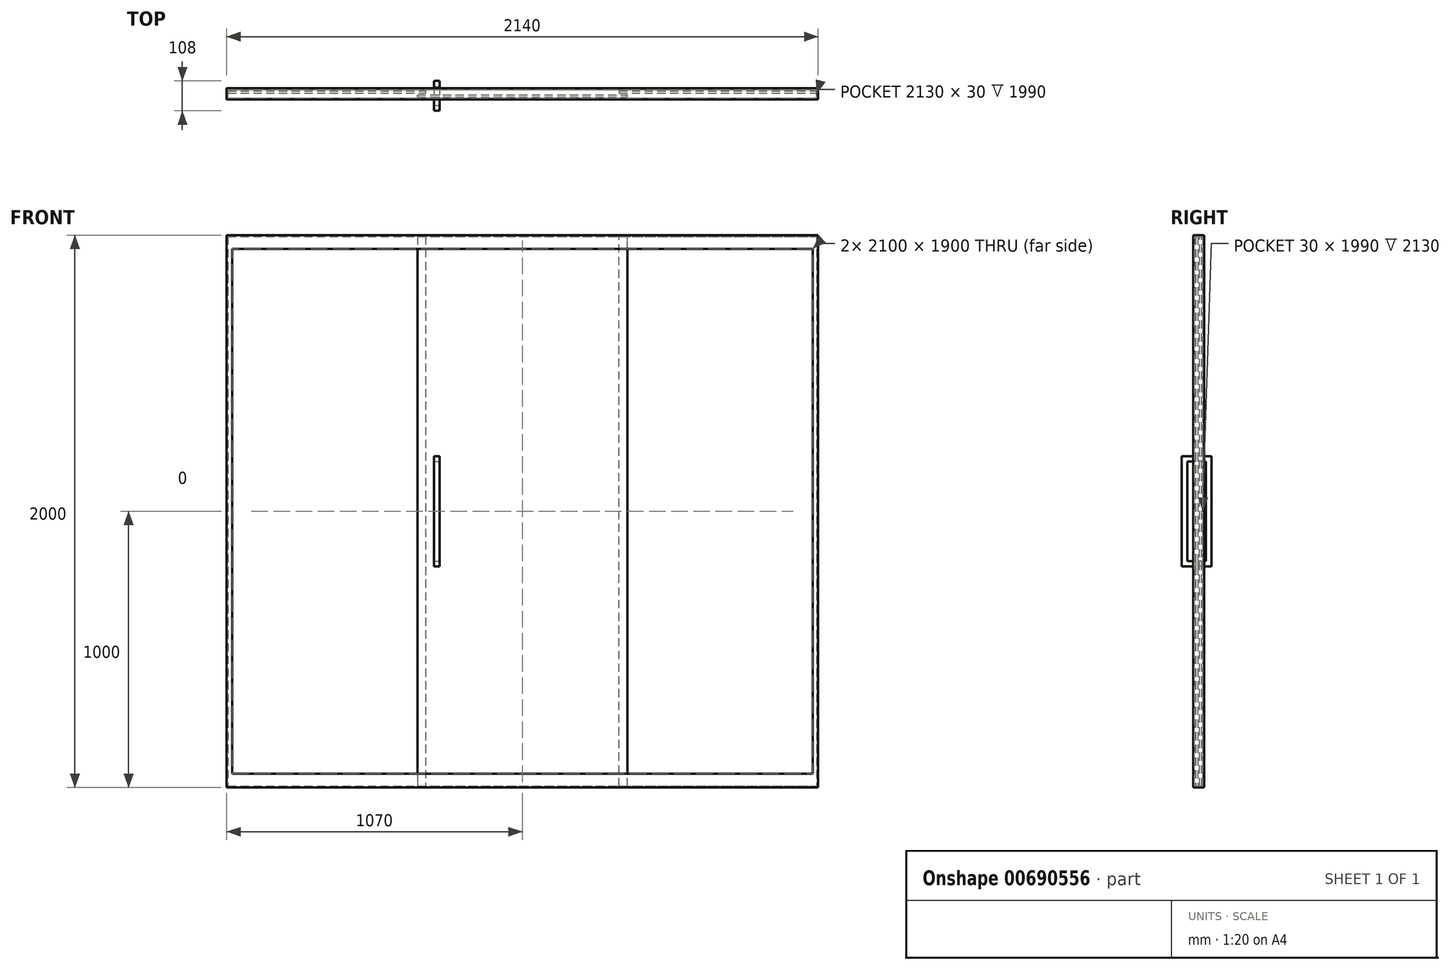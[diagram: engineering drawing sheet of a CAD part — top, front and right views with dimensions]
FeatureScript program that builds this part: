
annotation { "Feature Type Name" : "Feature", "Feature Type Description" : "" }
export const myFeature = defineFeature(function(context is Context, id is Id, definition is map)
    precondition{}
    {
        {
            var Q0;
            Q0=qCreatedBy(makeId("Front.planeOp"),FACE);
            var sketch = newSketch(context, id + "F0", { "sketchPlane" : qUnion([Q0])});
            skLineSegment(sketch, "E0.bottom", {"start": v(0, 0) * mm, "end": v(2140, 0) * mm});
            skLineSegment(sketch, "E0.top", {"start": v(0, 2000) * mm, "end": v(2140, 2000) * mm});
            skLineSegment(sketch, "E0.left", {"start": v(0, 0) * mm, "end": v(0, 2000) * mm});
            skLineSegment(sketch, "E0.right", {"start": v(2140, 0) * mm, "end": v(2140, 2000) * mm});
            skLineSegment(sketch, "E1.bottom", {"start": v(5, 1995) * mm, "end": v(2135, 1995) * mm});
            skLineSegment(sketch, "E1.top", {"start": v(5, 5) * mm, "end": v(2135, 5) * mm});
            skLineSegment(sketch, "E1.left", {"start": v(5, 1995) * mm, "end": v(5, 5) * mm});
            skLineSegment(sketch, "E1.right", {"start": v(2135, 1995) * mm, "end": v(2135, 5) * mm});
            skLineSegment(sketch, "E2.bottom", {"start": v(20, 1950) * mm, "end": v(2120, 1950) * mm});
            skLineSegment(sketch, "E2.top", {"start": v(20, 50) * mm, "end": v(2120, 50) * mm});
            skLineSegment(sketch, "E2.left", {"start": v(20, 1950) * mm, "end": v(20, 50) * mm});
            skLineSegment(sketch, "E2.right", {"start": v(2120, 1950) * mm, "end": v(2120, 50) * mm});
            skLineSegment(sketch, "E3", {"start": v(720, 1995) * mm, "end": v(720, 5) * mm});
            skLineSegment(sketch, "E4", {"start": v(1420, 5) * mm, "end": v(1420, 1995) * mm});
            skLineSegment(sketch, "E5", {"start": v(720, 1000) * mm, "end": v(5, 1000) * mm, "construction": true});
            skLineSegment(sketch, "E6", {"start": v(1420, 1000) * mm, "end": v(2135, 1000) * mm, "construction": true});
            skLineSegment(sketch, "E7", {"start": v(690, 1995) * mm, "end": v(690, 5) * mm});
            skLineSegment(sketch, "E8", {"start": v(1450, 5) * mm, "end": v(1450, 1995) * mm});
            skSolve(sketch);
        }
        {
            var Q0;
            {var subQ4=sQuery(id+"F0.wireOp",EDGE,"E1.left");Q0=makeQuery(id+"F0.imprint","IMPRINT",FACE,{"disambiguationData":[TD([[makeQuery(id+"F0.imprint","IMPRINT",EDGE,{"derivedFrom":subQ4}),1.0]])]});}
            var Q1;
            Q1=makeQuery(id+"F0.imprint","IMPRINT",FACE,{"disambiguationData":[TD([[makeQuery(id+"F0.imprint","IMPRINT",EDGE,{"derivedFrom":sQuery(id+"F0.wireOp",EDGE,"E0.bottom")}),1.0]])]});
            var Q2;
            {var subQ0=sQuery(id+"F0.wireOp",EDGE,"E3");var subQ1=sQuery(id+"F0.wireOp",EDGE,"E1.bottom");var subQ2=makeQuery(id+"F0.imprint","INTERSECT",VERTEX,{"derivedFrom":[subQ1,subQ0]});Q2=makeQuery(id+"F0.imprint","IMPRINT",FACE,{"disambiguationData":[TD([[makeQuery(id+"F0.imprint","IMPRINT",EDGE,{"disambiguationData":[TD([[subQ2,1.0]])],"derivedFrom":subQ1}),-1.0]])]});}
            var Q3;
            {var subQ0=sQuery(id+"F0.wireOp",EDGE,"E3");var subQ1=sQuery(id+"F0.wireOp",EDGE,"E1.bottom");var subQ2=makeQuery(id+"F0.imprint","INTERSECT",VERTEX,{"derivedFrom":[subQ1,subQ0]});Q3=makeQuery(id+"F0.imprint","IMPRINT",FACE,{"disambiguationData":[TD([[makeQuery(id+"F0.imprint","IMPRINT",EDGE,{"disambiguationData":[TD([[subQ2,-1.0]])],"derivedFrom":subQ1}),-1.0]])]});}
            var Q4;
            {var subQ4=sQuery(id+"F0.wireOp",EDGE,"E1.right");Q4=makeQuery(id+"F0.imprint","IMPRINT",FACE,{"disambiguationData":[TD([[makeQuery(id+"F0.imprint","IMPRINT",EDGE,{"derivedFrom":subQ4}),-1.0]])]});}
            var Q5;
            {var subQ0=sQuery(id+"F0.wireOp",EDGE,"E4");var subQ1=sQuery(id+"F0.wireOp",EDGE,"E1.bottom");var subQ2=makeQuery(id+"F0.imprint","INTERSECT",VERTEX,{"derivedFrom":[subQ1,subQ0]});Q5=makeQuery(id+"F0.imprint","IMPRINT",FACE,{"disambiguationData":[TD([[makeQuery(id+"F0.imprint","IMPRINT",EDGE,{"disambiguationData":[TD([[subQ2,-1.0]])],"derivedFrom":subQ1}),-1.0]])]});}
            var Q6;
            {var subQ0=sQuery(id+"F0.wireOp",EDGE,"E3");var subQ1=sQuery(id+"F0.wireOp",EDGE,"E1.top");var subQ2=makeQuery(id+"F0.imprint","INTERSECT",VERTEX,{"derivedFrom":[subQ1,subQ0]});Q6=makeQuery(id+"F0.imprint","IMPRINT",FACE,{"disambiguationData":[TD([[makeQuery(id+"F0.imprint","IMPRINT",EDGE,{"disambiguationData":[TD([[subQ2,1.0]])],"derivedFrom":subQ1}),1.0]])]});}
            var Q7;
            {var subQ0=sQuery(id+"F0.wireOp",EDGE,"E3");var subQ1=sQuery(id+"F0.wireOp",EDGE,"E1.top");var subQ2=makeQuery(id+"F0.imprint","INTERSECT",VERTEX,{"derivedFrom":[subQ1,subQ0]});Q7=makeQuery(id+"F0.imprint","IMPRINT",FACE,{"disambiguationData":[TD([[makeQuery(id+"F0.imprint","IMPRINT",EDGE,{"disambiguationData":[TD([[subQ2,-1.0]])],"derivedFrom":subQ1}),1.0]])]});}
            var Q8;
            {var subQ0=sQuery(id+"F0.wireOp",EDGE,"E4");var subQ1=sQuery(id+"F0.wireOp",EDGE,"E1.top");var subQ2=makeQuery(id+"F0.imprint","INTERSECT",VERTEX,{"derivedFrom":[subQ1,subQ0]});Q8=makeQuery(id+"F0.imprint","IMPRINT",FACE,{"disambiguationData":[TD([[makeQuery(id+"F0.imprint","IMPRINT",EDGE,{"disambiguationData":[TD([[subQ2,-1.0]])],"derivedFrom":subQ1}),1.0]])]});}
            extrude(context, id + "F1", {"entities" : qUnion([Q0, Q1, Q2, Q3, Q4, Q5, Q6, Q7, Q8]), "depth" : 20 * mm, "offsetDistance" : 25 * mm, "hasSecondDirection" : true, "secondDirectionOppositeDirection" : true, "secondDirectionDepth" : 20 * mm});
        }
        {
            var Q0;
            {var subQ4=sQuery(id+"F0.wireOp",EDGE,"E1.left");Q0=makeQuery(id+"F0.imprint","IMPRINT",FACE,{"disambiguationData":[TD([[makeQuery(id+"F0.imprint","IMPRINT",EDGE,{"derivedFrom":subQ4}),1.0]])]});}
            var Q1;
            {var subQ0=sQuery(id+"F0.wireOp",EDGE,"E3");var subQ1=sQuery(id+"F0.wireOp",EDGE,"E1.bottom");var subQ2=makeQuery(id+"F0.imprint","INTERSECT",VERTEX,{"derivedFrom":[subQ1,subQ0]});Q1=makeQuery(id+"F0.imprint","IMPRINT",FACE,{"disambiguationData":[TD([[makeQuery(id+"F0.imprint","IMPRINT",EDGE,{"disambiguationData":[TD([[subQ2,1.0]])],"derivedFrom":subQ1}),-1.0]])]});}
            var Q2;
            {var subQ0=sQuery(id+"F0.wireOp",EDGE,"E3");var subQ1=sQuery(id+"F0.wireOp",EDGE,"E1.bottom");var subQ2=makeQuery(id+"F0.imprint","INTERSECT",VERTEX,{"derivedFrom":[subQ1,subQ0]});Q2=makeQuery(id+"F0.imprint","IMPRINT",FACE,{"disambiguationData":[TD([[makeQuery(id+"F0.imprint","IMPRINT",EDGE,{"disambiguationData":[TD([[subQ2,-1.0]])],"derivedFrom":subQ1}),-1.0]])]});}
            var Q3;
            {var subQ0=sQuery(id+"F0.wireOp",EDGE,"E4");var subQ1=sQuery(id+"F0.wireOp",EDGE,"E1.bottom");var subQ2=makeQuery(id+"F0.imprint","INTERSECT",VERTEX,{"derivedFrom":[subQ1,subQ0]});Q3=makeQuery(id+"F0.imprint","IMPRINT",FACE,{"disambiguationData":[TD([[makeQuery(id+"F0.imprint","IMPRINT",EDGE,{"disambiguationData":[TD([[subQ2,-1.0]])],"derivedFrom":subQ1}),-1.0]])]});}
            var Q4;
            {var subQ4=sQuery(id+"F0.wireOp",EDGE,"E1.right");Q4=makeQuery(id+"F0.imprint","IMPRINT",FACE,{"disambiguationData":[TD([[makeQuery(id+"F0.imprint","IMPRINT",EDGE,{"derivedFrom":subQ4}),-1.0]])]});}
            var Q5;
            {var subQ0=sQuery(id+"F0.wireOp",EDGE,"E3");var subQ1=sQuery(id+"F0.wireOp",EDGE,"E1.top");var subQ2=makeQuery(id+"F0.imprint","INTERSECT",VERTEX,{"derivedFrom":[subQ1,subQ0]});Q5=makeQuery(id+"F0.imprint","IMPRINT",FACE,{"disambiguationData":[TD([[makeQuery(id+"F0.imprint","IMPRINT",EDGE,{"disambiguationData":[TD([[subQ2,1.0]])],"derivedFrom":subQ1}),1.0]])]});}
            var Q6;
            {var subQ0=sQuery(id+"F0.wireOp",EDGE,"E3");var subQ1=sQuery(id+"F0.wireOp",EDGE,"E1.top");var subQ2=makeQuery(id+"F0.imprint","INTERSECT",VERTEX,{"derivedFrom":[subQ1,subQ0]});Q6=makeQuery(id+"F0.imprint","IMPRINT",FACE,{"disambiguationData":[TD([[makeQuery(id+"F0.imprint","IMPRINT",EDGE,{"disambiguationData":[TD([[subQ2,-1.0]])],"derivedFrom":subQ1}),1.0]])]});}
            var Q7;
            {var subQ0=sQuery(id+"F0.wireOp",EDGE,"E4");var subQ1=sQuery(id+"F0.wireOp",EDGE,"E1.top");var subQ2=makeQuery(id+"F0.imprint","INTERSECT",VERTEX,{"derivedFrom":[subQ1,subQ0]});Q7=makeQuery(id+"F0.imprint","IMPRINT",FACE,{"disambiguationData":[TD([[makeQuery(id+"F0.imprint","IMPRINT",EDGE,{"disambiguationData":[TD([[subQ2,-1.0]])],"derivedFrom":subQ1}),1.0]])]});}
            extrude(context, id + "F2", {"entities" : qUnion([Q0, Q1, Q2, Q3, Q4, Q5, Q6, Q7]), "operationType" : NewBodyOperationType.REMOVE, "depth" : 15 * mm, "offsetDistance" : 25 * mm, "hasSecondDirection" : true, "secondDirectionOppositeDirection" : true, "secondDirectionDepth" : 15 * mm});
        }
        {
            var Q0;
            {var subQ0=sQuery(id+"F0.wireOp",EDGE,"E2.left");Q0=makeQuery(id+"F0.imprint","IMPRINT",FACE,{"disambiguationData":[TD([[makeQuery(id+"F0.imprint","IMPRINT",EDGE,{"derivedFrom":subQ0}),1.0]])]});}
            var Q1;
            {var subQ0=sQuery(id+"F0.wireOp",EDGE,"E2.right");Q1=makeQuery(id+"F0.imprint","IMPRINT",FACE,{"disambiguationData":[TD([[makeQuery(id+"F0.imprint","IMPRINT",EDGE,{"derivedFrom":subQ0}),-1.0]])]});}
            var Q2;
            {var subQ4=sQuery(id+"F0.wireOp",EDGE,"E1.right");Q2=makeQuery(id+"F0.imprint","IMPRINT",FACE,{"disambiguationData":[TD([[makeQuery(id+"F0.imprint","IMPRINT",EDGE,{"derivedFrom":subQ4}),-1.0]])]});}
            var Q3;
            {var subQ4=sQuery(id+"F0.wireOp",EDGE,"E1.left");Q3=makeQuery(id+"F0.imprint","IMPRINT",FACE,{"disambiguationData":[TD([[makeQuery(id+"F0.imprint","IMPRINT",EDGE,{"derivedFrom":subQ4}),1.0]])]});}
            var Q4;
            {var subQ0=sQuery(id+"F0.wireOp",EDGE,"E3");var subQ1=sQuery(id+"F0.wireOp",EDGE,"E1.bottom");var subQ2=makeQuery(id+"F0.imprint","INTERSECT",VERTEX,{"derivedFrom":[subQ1,subQ0]});Q4=makeQuery(id+"F0.imprint","IMPRINT",FACE,{"disambiguationData":[TD([[makeQuery(id+"F0.imprint","IMPRINT",EDGE,{"disambiguationData":[TD([[subQ2,1.0]])],"derivedFrom":subQ1}),-1.0]])]});}
            var Q5;
            {var subQ0=sQuery(id+"F0.wireOp",EDGE,"E7");var subQ1=sQuery(id+"F0.wireOp",EDGE,"E2.bottom");var subQ2=makeQuery(id+"F0.imprint","INTERSECT",VERTEX,{"derivedFrom":[subQ1,subQ0]});Q5=makeQuery(id+"F0.imprint","IMPRINT",FACE,{"disambiguationData":[TD([[makeQuery(id+"F0.imprint","IMPRINT",EDGE,{"disambiguationData":[TD([[subQ2,-1.0]])],"derivedFrom":subQ1}),-1.0]])]});}
            var Q6;
            {var subQ0=sQuery(id+"F0.wireOp",EDGE,"E4");var subQ1=sQuery(id+"F0.wireOp",EDGE,"E1.bottom");var subQ2=makeQuery(id+"F0.imprint","INTERSECT",VERTEX,{"derivedFrom":[subQ1,subQ0]});Q6=makeQuery(id+"F0.imprint","IMPRINT",FACE,{"disambiguationData":[TD([[makeQuery(id+"F0.imprint","IMPRINT",EDGE,{"disambiguationData":[TD([[subQ2,-1.0]])],"derivedFrom":subQ1}),-1.0]])]});}
            var Q7;
            {var subQ0=sQuery(id+"F0.wireOp",EDGE,"E4");var subQ1=sQuery(id+"F0.wireOp",EDGE,"E2.bottom");var subQ2=makeQuery(id+"F0.imprint","INTERSECT",VERTEX,{"derivedFrom":[subQ1,subQ0]});Q7=makeQuery(id+"F0.imprint","IMPRINT",FACE,{"disambiguationData":[TD([[makeQuery(id+"F0.imprint","IMPRINT",EDGE,{"disambiguationData":[TD([[subQ2,-1.0]])],"derivedFrom":subQ1}),-1.0]])]});}
            var Q8;
            {var subQ0=sQuery(id+"F0.wireOp",EDGE,"E4");var subQ1=sQuery(id+"F0.wireOp",EDGE,"E1.top");var subQ2=makeQuery(id+"F0.imprint","INTERSECT",VERTEX,{"derivedFrom":[subQ1,subQ0]});Q8=makeQuery(id+"F0.imprint","IMPRINT",FACE,{"disambiguationData":[TD([[makeQuery(id+"F0.imprint","IMPRINT",EDGE,{"disambiguationData":[TD([[subQ2,-1.0]])],"derivedFrom":subQ1}),1.0]])]});}
            var Q9;
            {var subQ0=sQuery(id+"F0.wireOp",EDGE,"E3");var subQ1=sQuery(id+"F0.wireOp",EDGE,"E1.top");var subQ2=makeQuery(id+"F0.imprint","INTERSECT",VERTEX,{"derivedFrom":[subQ1,subQ0]});Q9=makeQuery(id+"F0.imprint","IMPRINT",FACE,{"disambiguationData":[TD([[makeQuery(id+"F0.imprint","IMPRINT",EDGE,{"disambiguationData":[TD([[subQ2,1.0]])],"derivedFrom":subQ1}),1.0]])]});}
            extrude(context, id + "F3", {"entities" : qUnion([Q0, Q1, Q2, Q3, Q4, Q5, Q6, Q7, Q8, Q9]), "oppositeDirection" : true, "depth" : 11 * mm, "offsetDistance" : 25 * mm, "hasSecondDirection" : true, "secondDirectionOppositeDirection" : true, "secondDirectionDepth" : 3 * mm});
        }
        {
            var Q0;
            {var subQ0=sQuery(id+"F0.wireOp",EDGE,"E3");var subQ1=sQuery(id+"F0.wireOp",EDGE,"E1.bottom");var subQ2=makeQuery(id+"F0.imprint","INTERSECT",VERTEX,{"derivedFrom":[subQ1,subQ0]});Q0=makeQuery(id+"F0.imprint","IMPRINT",FACE,{"disambiguationData":[TD([[makeQuery(id+"F0.imprint","IMPRINT",EDGE,{"disambiguationData":[TD([[subQ2,-1.0]])],"derivedFrom":subQ1}),-1.0]])]});}
            var Q1;
            {var subQ0=sQuery(id+"F0.wireOp",EDGE,"E3");var subQ1=sQuery(id+"F0.wireOp",EDGE,"E2.bottom");var subQ2=makeQuery(id+"F0.imprint","INTERSECT",VERTEX,{"derivedFrom":[subQ1,subQ0]});Q1=makeQuery(id+"F0.imprint","IMPRINT",FACE,{"disambiguationData":[TD([[makeQuery(id+"F0.imprint","IMPRINT",EDGE,{"disambiguationData":[TD([[subQ2,-1.0]])],"derivedFrom":subQ1}),-1.0]])]});}
            var Q2;
            {var subQ0=sQuery(id+"F0.wireOp",EDGE,"E4");var subQ1=sQuery(id+"F0.wireOp",EDGE,"E1.bottom");var subQ2=makeQuery(id+"F0.imprint","INTERSECT",VERTEX,{"derivedFrom":[subQ1,subQ0]});Q2=makeQuery(id+"F0.imprint","IMPRINT",FACE,{"disambiguationData":[TD([[makeQuery(id+"F0.imprint","IMPRINT",EDGE,{"disambiguationData":[TD([[subQ2,-1.0]])],"derivedFrom":subQ1}),-1.0]])]});}
            var Q3;
            {var subQ0=sQuery(id+"F0.wireOp",EDGE,"E4");var subQ1=sQuery(id+"F0.wireOp",EDGE,"E2.bottom");var subQ2=makeQuery(id+"F0.imprint","INTERSECT",VERTEX,{"derivedFrom":[subQ1,subQ0]});Q3=makeQuery(id+"F0.imprint","IMPRINT",FACE,{"disambiguationData":[TD([[makeQuery(id+"F0.imprint","IMPRINT",EDGE,{"disambiguationData":[TD([[subQ2,-1.0]])],"derivedFrom":subQ1}),-1.0]])]});}
            var Q4;
            {var subQ0=sQuery(id+"F0.wireOp",EDGE,"E3");var subQ1=sQuery(id+"F0.wireOp",EDGE,"E1.bottom");var subQ2=makeQuery(id+"F0.imprint","INTERSECT",VERTEX,{"derivedFrom":[subQ1,subQ0]});Q4=makeQuery(id+"F0.imprint","IMPRINT",FACE,{"disambiguationData":[TD([[makeQuery(id+"F0.imprint","IMPRINT",EDGE,{"disambiguationData":[TD([[subQ2,1.0]])],"derivedFrom":subQ1}),-1.0]])]});}
            var Q5;
            {var subQ0=sQuery(id+"F0.wireOp",EDGE,"E7");var subQ1=sQuery(id+"F0.wireOp",EDGE,"E2.bottom");var subQ2=makeQuery(id+"F0.imprint","INTERSECT",VERTEX,{"derivedFrom":[subQ1,subQ0]});Q5=makeQuery(id+"F0.imprint","IMPRINT",FACE,{"disambiguationData":[TD([[makeQuery(id+"F0.imprint","IMPRINT",EDGE,{"disambiguationData":[TD([[subQ2,-1.0]])],"derivedFrom":subQ1}),-1.0]])]});}
            var Q6;
            {var subQ0=sQuery(id+"F0.wireOp",EDGE,"E3");var subQ1=sQuery(id+"F0.wireOp",EDGE,"E1.top");var subQ2=makeQuery(id+"F0.imprint","INTERSECT",VERTEX,{"derivedFrom":[subQ1,subQ0]});Q6=makeQuery(id+"F0.imprint","IMPRINT",FACE,{"disambiguationData":[TD([[makeQuery(id+"F0.imprint","IMPRINT",EDGE,{"disambiguationData":[TD([[subQ2,1.0]])],"derivedFrom":subQ1}),1.0]])]});}
            var Q7;
            {var subQ0=sQuery(id+"F0.wireOp",EDGE,"E3");var subQ1=sQuery(id+"F0.wireOp",EDGE,"E1.top");var subQ2=makeQuery(id+"F0.imprint","INTERSECT",VERTEX,{"derivedFrom":[subQ1,subQ0]});Q7=makeQuery(id+"F0.imprint","IMPRINT",FACE,{"disambiguationData":[TD([[makeQuery(id+"F0.imprint","IMPRINT",EDGE,{"disambiguationData":[TD([[subQ2,-1.0]])],"derivedFrom":subQ1}),1.0]])]});}
            var Q8;
            {var subQ0=sQuery(id+"F0.wireOp",EDGE,"E4");var subQ1=sQuery(id+"F0.wireOp",EDGE,"E1.top");var subQ2=makeQuery(id+"F0.imprint","INTERSECT",VERTEX,{"derivedFrom":[subQ1,subQ0]});Q8=makeQuery(id+"F0.imprint","IMPRINT",FACE,{"disambiguationData":[TD([[makeQuery(id+"F0.imprint","IMPRINT",EDGE,{"disambiguationData":[TD([[subQ2,-1.0]])],"derivedFrom":subQ1}),1.0]])]});}
            extrude(context, id + "F4", {"entities" : qUnion([Q0, Q1, Q2, Q3, Q4, Q5, Q6, Q7, Q8]), "depth" : 11 * mm, "offsetDistance" : 25 * mm, "hasSecondDirection" : true, "secondDirectionOppositeDirection" : false, "secondDirectionDepth" : 3 * mm});
        }
        {
            var Q0;
            Q0=makeQuery(id+"F4.opExtrude","CAP_FACE",FACE,{"disambiguationData":[OSD([sQuery(id+"F0.wireOp",EDGE,"E1.bottom"),sQuery(id+"F0.wireOp",EDGE,"E1.top"),sQuery(id+"F0.wireOp",EDGE,"E7"),sQuery(id+"F0.wireOp",EDGE,"E8")])],"isStart":false});
            var sketch = newSketch(context, id + "F5", { "sketchPlane" : qUnion([Q0])});
            skLineSegment(sketch, "E9.bottom", {"start": v(750, 1200) * mm, "end": v(770, 1200) * mm});
            skLineSegment(sketch, "E9.top", {"start": v(750, 1180) * mm, "end": v(770, 1180) * mm});
            skLineSegment(sketch, "E9.left", {"start": v(750, 1200) * mm, "end": v(750, 1180) * mm});
            skLineSegment(sketch, "E9.right", {"start": v(770, 1200) * mm, "end": v(770, 1180) * mm});
            skLineSegment(sketch, "E10.bottom", {"start": v(750, 820) * mm, "end": v(770, 820) * mm});
            skLineSegment(sketch, "E10.top", {"start": v(750, 800) * mm, "end": v(770, 800) * mm});
            skLineSegment(sketch, "E10.left", {"start": v(750, 820) * mm, "end": v(750, 800) * mm});
            skLineSegment(sketch, "E10.right", {"start": v(770, 820) * mm, "end": v(770, 800) * mm});
            skLineSegment(sketch, "E11", {"start": v(750, 1180) * mm, "end": v(750, 820) * mm});
            skLineSegment(sketch, "E12", {"start": v(770, 1180) * mm, "end": v(770, 820) * mm});
            skLineSegment(sketch, "E13", {"start": v(750, 1000) * mm, "end": v(750, 0) * mm, "construction": true});
            skLineSegment(sketch, "E14", {"start": v(750, 0) * mm, "end": v(0, 0) * mm, "construction": true});
            skSolve(sketch);
        }
        {
            var Q0;
            Q0=makeQuery(id+"F5.imprint","IMPRINT",FACE,{"disambiguationData":[TD([[makeQuery(id+"F5.imprint","IMPRINT",EDGE,{"derivedFrom":sQuery(id+"F5.wireOp",EDGE,"E9.bottom")}),-1.0]])]});
            var Q1;
            Q1=makeQuery(id+"F5.imprint","IMPRINT",FACE,{"disambiguationData":[TD([[makeQuery(id+"F5.imprint","IMPRINT",EDGE,{"derivedFrom":sQuery(id+"F5.wireOp",EDGE,"E10.bottom")}),-1.0]])]});
            extrude(context, id + "F6", {"entities" : qUnion([Q0, Q1]), "depth" : 50 * mm, "offsetDistance" : 25 * mm});
        }
        {
            var Q0;
            Q0=makeQuery(id+"F5.imprint","IMPRINT",FACE,{"disambiguationData":[TD([[makeQuery(id+"F5.imprint","IMPRINT",EDGE,{"derivedFrom":sQuery(id+"F5.wireOp",EDGE,"E9.top")}),-1.0]])]});
            extrude(context, id + "F7", {"entities" : qUnion([Q0]), "operationType" : NewBodyOperationType.ADD, "depth" : 50 * mm, "offsetDistance" : 25 * mm, "hasSecondDirection" : true, "secondDirectionOppositeDirection" : false, "secondDirectionDepth" : 30 * mm});
        }
        {
            var Q0;
            Q0=makeQuery(id+"F5.imprint","IMPRINT",FACE,{"disambiguationData":[TD([[makeQuery(id+"F5.imprint","IMPRINT",EDGE,{"derivedFrom":sQuery(id+"F5.wireOp",EDGE,"E9.bottom")}),1.0]])]});
            cPlane(context, id + "F8", {"entities" : qUnion([Q0]), "cplaneType" : CPlaneType.OFFSET, "offset" : 4 * mm, "oppositeDirection" : true, "width" : 150 * mm, "height" : 150 * mm});
        }
        {
            var Q0;
            Q0=makeQuery(id+"F6.opExtrude","SWEPT_BODY",BODY,{"disambiguationData":[OSD([sQuery(id+"F5.wireOp",EDGE,"E9.bottom"),sQuery(id+"F5.wireOp",EDGE,"E9.top"),sQuery(id+"F5.wireOp",EDGE,"E9.left"),sQuery(id+"F5.wireOp",EDGE,"E9.right")])]});
            var Q1;
            Q1=qCreatedBy(id+"F8.planeOp",FACE);
            mirror(context, id + "F9", {"entities" : qUnion([Q0]), "mirrorPlane" : qUnion([Q1])});
        }
    });
